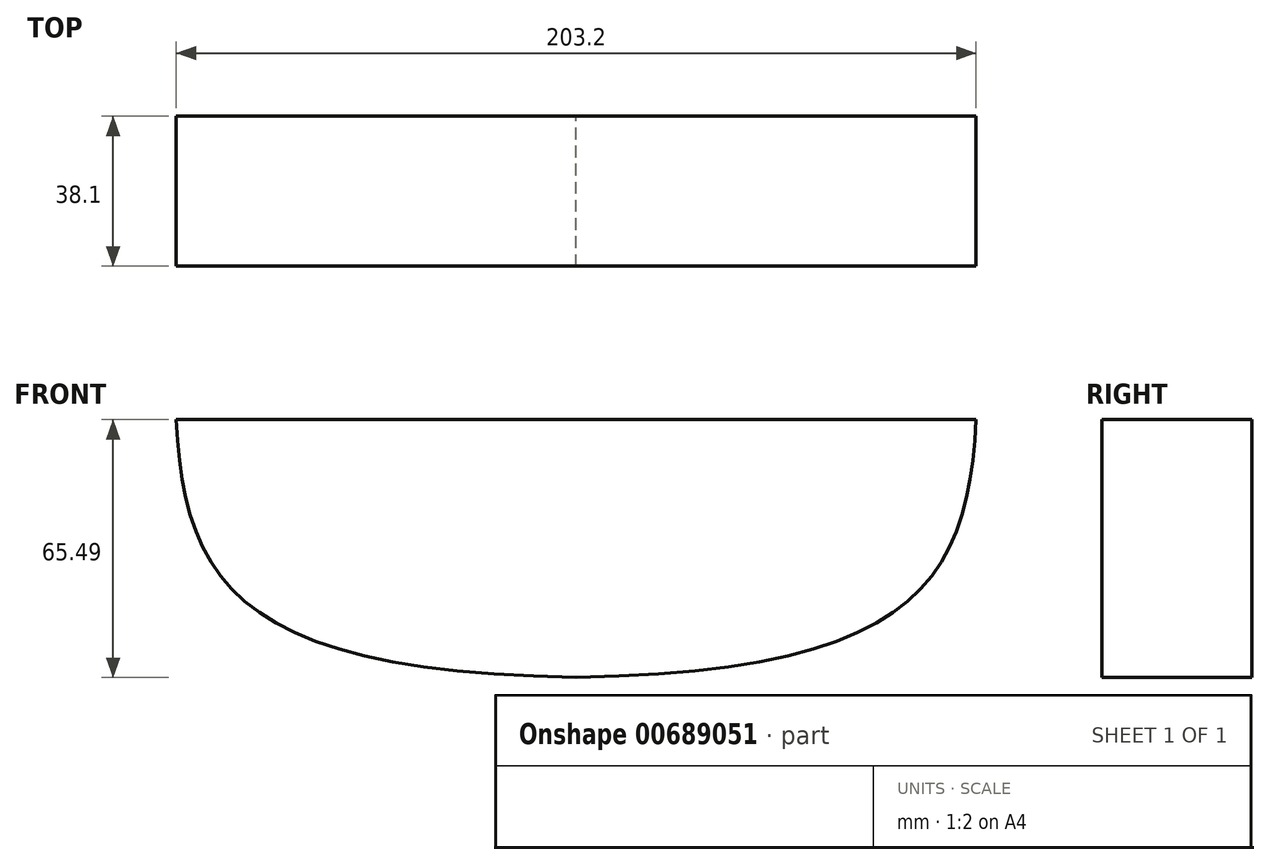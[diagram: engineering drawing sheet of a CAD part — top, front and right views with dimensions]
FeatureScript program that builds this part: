
annotation { "Feature Type Name" : "Feature", "Feature Type Description" : "" }
export const myFeature = defineFeature(function(context is Context, id is Id, definition is map)
    precondition{}
    {
        {
            var Q0;
            Q0=qCreatedBy(makeId("Front.planeOp"),FACE);
            var sketch = newSketch(context, id + "F0", { "sketchPlane" : qUnion([Q0])});
            skLineSegment(sketch, "E0", {"start": v(-101.6, 0) * mm, "end": v(101.6, 0) * mm});
            skLineSegment(sketch, "E1", {"start": v(-82.55, 218.44) * mm, "end": v(82.55, 218.44) * mm});
            skLineSegment(sketch, "E2", {"start": v(0, -65.49) * mm, "end": v(0, 290.11) * mm});
            skFitSpline(sketch, "E3", {"points": [v(-101.6, 0) * mm, v(-75.42, 74.59) * mm, v(0, 112.31) * mm, v(75.2, 158.26) * mm, v(82.55, 218.44) * mm], "startDerivative": vector(-25.74, 351.6) * mm, "endDerivative": vector(-16.4, 281.8) * mm});
            skFitSpline(sketch, "E4", {"points": [v(0, 0) * mm, v(-47.25, 44.36) * mm, v(0, 91.94) * mm, v(22.32, 103.68) * mm, v(67.13, 139.67) * mm, v(82.55, 218.44) * mm], "startDerivative": vector(-499.11, 79.46) * mm, "endDerivative": vector(-84.9, 342.35) * mm});
            skFitSpline(sketch, "E5.MirrorCS", {"points": [v(0, 0) * mm, v(47.25, 44.36) * mm, v(0, 91.94) * mm, v(-22.32, 103.68) * mm, v(-67.13, 139.67) * mm, v(-82.55, 218.44) * mm], "startDerivative": vector(499.11, 79.46) * mm, "endDerivative": vector(84.9, 342.35) * mm});
            skFitSpline(sketch, "E6.MirrorCS", {"points": [v(101.6, 0) * mm, v(75.42, 74.59) * mm, v(0, 112.31) * mm, v(-75.2, 158.26) * mm, v(-82.55, 218.44) * mm], "startDerivative": vector(25.74, 351.6) * mm, "endDerivative": vector(16.4, 281.8) * mm});
            skFitSpline(sketch, "E7", {"points": [v(101.6, 0) * mm, v(0, -65.49) * mm], "startDerivative": vector(-6.32, -123.6) * mm, "endDerivative": vector(-259.26, -4.59) * mm});
            skFitSpline(sketch, "E8.MirrorCS", {"points": [v(-101.6, 0) * mm, v(0, -65.49) * mm], "startDerivative": vector(6.32, -123.6) * mm, "endDerivative": vector(259.26, -4.59) * mm});
            skSolve(sketch);
        }
        {
            var Q0;
            {var subQ0=sQuery(id+"F0.wireOp",EDGE,"E8.MirrorCS");Q0=makeQuery(id+"F0.imprint","IMPRINT",FACE,{"disambiguationData":[TD([[makeQuery(id+"F0.imprint","IMPRINT",EDGE,{"derivedFrom":subQ0}),1.0]])]});}
            var Q1;
            {var subQ0=sQuery(id+"F0.wireOp",EDGE,"E7");Q1=makeQuery(id+"F0.imprint","IMPRINT",FACE,{"disambiguationData":[TD([[makeQuery(id+"F0.imprint","IMPRINT",EDGE,{"derivedFrom":subQ0}),-1.0]])]});}
            extrude(context, id + "F1", {"entities" : qUnion([Q0, Q1]), "depth" : 38.1 * mm, "offsetDistance" : 25.4 * mm});
        }
    });
